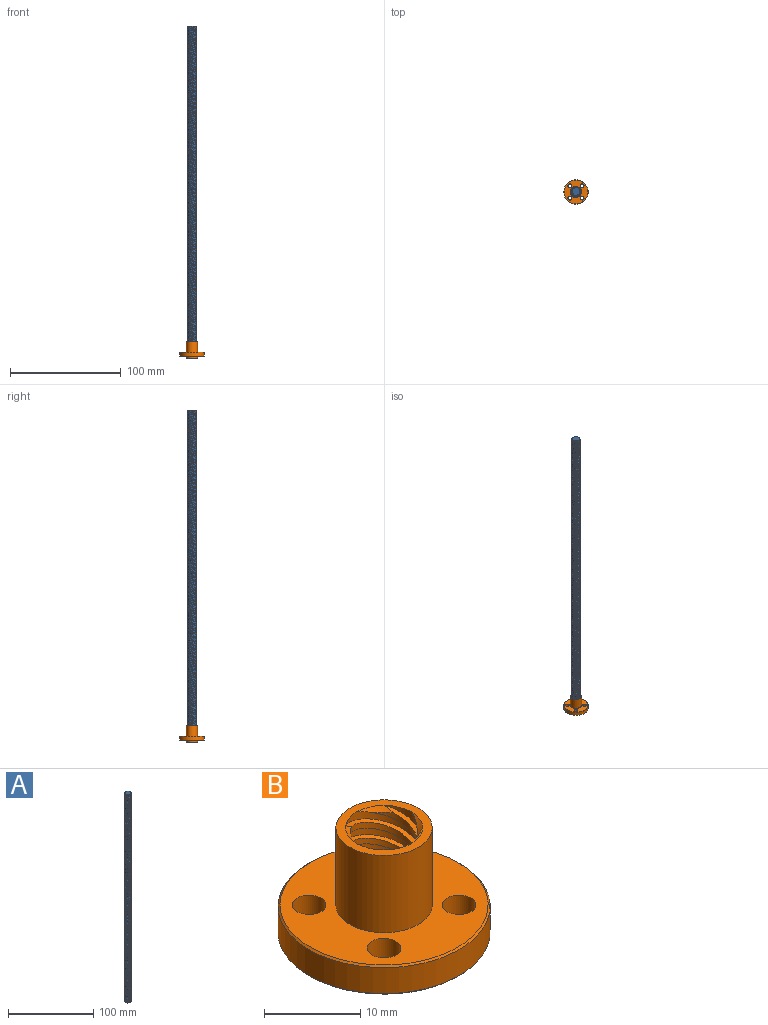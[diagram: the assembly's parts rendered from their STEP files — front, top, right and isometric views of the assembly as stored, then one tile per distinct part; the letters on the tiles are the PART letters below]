
ASSEMBLY  parts=2 mates=1
PART A: 26 faces, bbox 2094x2094x581.3 mm
  f0: cone r=4mm half-angle=45deg, axis (0,0,1), area 2.4mm2, adj f3,f18,f19,f23
  f1: cylinder r=4mm len=299mm, axis (0,0,-1), area 943.4mm2, adj f5,f6,f8,f9
  f2: cone r=3.5mm half-angle=45deg, axis (0,0,-1), area 2.3mm2, adj f3,f19,f20,f23
  f3: bspline ~301.13x8mm, area 482.1mm2, adj f0,f2,f4,f19
  f4: cylinder r=3.5mm len=300mm, axis (0,0,1), area 792.2mm2, adj f3,f5,f18,f20
  f5: bspline ~1051.52x581.26mm, area 480.4mm2, adj f1,f4,f6,f8
  f6: cone r=4mm half-angle=45deg, axis (0,0,1), area 2.4mm2, adj f1,f5,f9,f18
  f7: cylinder r=4mm len=299mm, axis (0,0,-1), area 943.4mm2, adj f11,f12,f14,f15
  f8: cone r=3.5mm half-angle=45deg, axis (0,0,-1), area 2.3mm2, adj f1,f5,f9,f20
  f9: bspline ~301.13x8mm, area 482.1mm2, adj f1,f6,f8,f10
  f10: cylinder r=3.5mm len=300mm, axis (0,0,1), area 792.2mm2, adj f9,f11,f18,f20
  f11: bspline ~1051.52x581.26mm, area 480.4mm2, adj f7,f10,f12,f14
  f12: cone r=4mm half-angle=45deg, axis (0,0,1), area 2.4mm2, adj f7,f11,f15,f18
  f13: cylinder r=4mm len=299mm, axis (0,0,-1), area 943.4mm2, adj f17,f22,f24,f25
  f14: cone r=3.5mm half-angle=45deg, axis (0,0,-1), area 2.3mm2, adj f7,f11,f15,f20
  f15: bspline ~301.13x8mm, area 482.1mm2, adj f7,f12,f14,f16
  f16: cylinder r=3.5mm len=300mm, axis (0,0,1), area 792.2mm2, adj f15,f17,f18,f20
  f17: bspline ~1051.52x581.26mm, area 480.4mm2, adj f13,f16,f24,f25
  f18: plane 7x7mm, normal (0,0,-1), area 38.5mm2, adj f0,f4,f6,f10,f12,f16,f21,f25
  f19: cylinder r=4mm len=299mm, axis (0,0,-1), area 943.4mm2, adj f0,f2,f3,f23
  f20: plane 7x7mm, normal (0,0,1), area 38.5mm2, adj f2,f4,f8,f10,f14,f16,f21,f24
  f21: cylinder r=3.5mm len=300mm, axis (0,0,1), area 792.2mm2, adj f18,f20,f22,f23
  f22: bspline ~301.13x8mm, area 482.1mm2, adj f13,f21,f24,f25
  f23: bspline ~1051.52x581.26mm, area 480.4mm2, adj f0,f2,f19,f21
  f24: cone r=3.5mm half-angle=45deg, axis (0,0,-1), area 2.3mm2, adj f13,f17,f20,f22
  f25: cone r=4mm half-angle=45deg, axis (0,0,1), area 2.4mm2, adj f13,f17,f18,f22
PART B: 37 faces, bbox 22x22x16.4 mm
  f0: cylinder r=1.75mm len=3.7mm, axis (0,0,-1), area 40.7mm2, adj f5,f6
  f1: cylinder r=1.75mm len=3.7mm, axis (0,0,-1), area 40.7mm2, adj f5,f6
  f2: cylinder r=1.75mm len=3.7mm, axis (0,0,-1), area 40.7mm2, adj f5,f6
  f3: cylinder r=1.75mm len=3.7mm, axis (0,0,-1), area 40.7mm2, adj f5,f6
  f4: cylinder r=11mm len=22mm, axis (0,0,-1), area 228.1mm2, adj f27,f28
  f5: plane 21.6x21.6mm, normal (0,0,1), area 249.4mm2, adj f0,f1,f2,f3,f9,f28
  f6: plane 21.6x21.6mm, normal (0,0,-1), area 249.4mm2, adj f0,f1,f2,f3,f8,f27
  f7: plane 10x10mm, normal (0,0,-1), area 28.3mm2, adj f8,f11,f15,f19,f23,f29,f30,f31
  f8: cylinder r=5mm len=10mm, axis (0,0,-1), area 47.1mm2, adj f6,f7
  f9: cylinder r=5mm len=10mm, axis (0,0,-1), area 307.9mm2, adj f5,f10
  f10: plane 10x10mm, normal (0,0,1), area 28.3mm2, adj f9,f11,f15,f19,f23,f33,f34,f35
  f11: cylinder r=4mm len=15mm, axis (0,0,-1), area 47.1mm2, adj f7,f10,f14,f16
  f12: bspline ~16.13x8mm, area 23.3mm2, adj f13,f23,f30,f36
  f13: cylinder r=3.5mm len=14mm, axis (0,0,1), area 28.2mm2, adj f12,f14,f30,f36
  f14: bspline ~16.4x9mm, area 23.3mm2, adj f11,f13,f30,f36
  f15: cylinder r=4mm len=15mm, axis (0,0,-1), area 47.1mm2, adj f7,f10,f18,f20
  f16: bspline ~16.13x8mm, area 23.3mm2, adj f11,f17,f29,f35
  f17: cylinder r=3.5mm len=14mm, axis (0,0,1), area 28.2mm2, adj f16,f18,f29,f35
  f18: bspline ~16.4x9mm, area 23.3mm2, adj f15,f17,f29,f35
  f19: cylinder r=4mm len=15mm, axis (0,0,-1), area 47.1mm2, adj f7,f10,f22,f25
  f20: bspline ~16.13x8mm, area 23.3mm2, adj f15,f21,f32,f34
  f21: cylinder r=3.5mm len=14mm, axis (0,0,1), area 28.2mm2, adj f20,f22,f32,f34
  f22: bspline ~16.4x9mm, area 23.3mm2, adj f19,f21,f32,f34
  f23: cylinder r=4mm len=15mm, axis (0,0,-1), area 47.1mm2, adj f7,f10,f12,f26
  f24: cylinder r=3.5mm len=14mm, axis (0,0,1), area 28.2mm2, adj f25,f26,f31,f33
  f25: bspline ~16.13x8mm, area 23.3mm2, adj f19,f24,f31,f33
  f26: bspline ~16.4x9mm, area 23.3mm2, adj f23,f24,f31,f33
  f27: cone r=11mm half-angle=45deg, axis (0,0,1), area 19.4mm2, adj f4,f6
  f28: cone r=10.8mm half-angle=45deg, axis (0,0,-1), area 19.4mm2, adj f4,f5
  f29: cone r=4mm half-angle=45deg, axis (0,0,-1), area 1.8mm2, adj f7,f16,f17,f18
  f30: cone r=4mm half-angle=45deg, axis (0,0,-1), area 1.8mm2, adj f7,f12,f13,f14
  f31: cone r=4mm half-angle=45deg, axis (0,0,-1), area 1.8mm2, adj f7,f24,f25,f26
  f32: cone r=4mm half-angle=45deg, axis (0,0,-1), area 1.8mm2, adj f7,f20,f21,f22
  f33: cone r=3.5mm half-angle=45deg, axis (0,0,1), area 1.8mm2, adj f10,f24,f25,f26
  f34: cone r=3.5mm half-angle=45deg, axis (0,0,1), area 1.8mm2, adj f10,f20,f21,f22
  f35: cone r=3.5mm half-angle=45deg, axis (0,0,1), area 1.8mm2, adj f10,f16,f17,f18
  f36: cone r=3.5mm half-angle=45deg, axis (0,0,1), area 1.8mm2, adj f10,f12,f13,f14
PLACE A t=(0,0,6.5)mm
PLACE B at identity fixed
MATE cylindrical A.f0 <-> B.f4  axis (0,0,-1) through (0,0,6.5)mm
